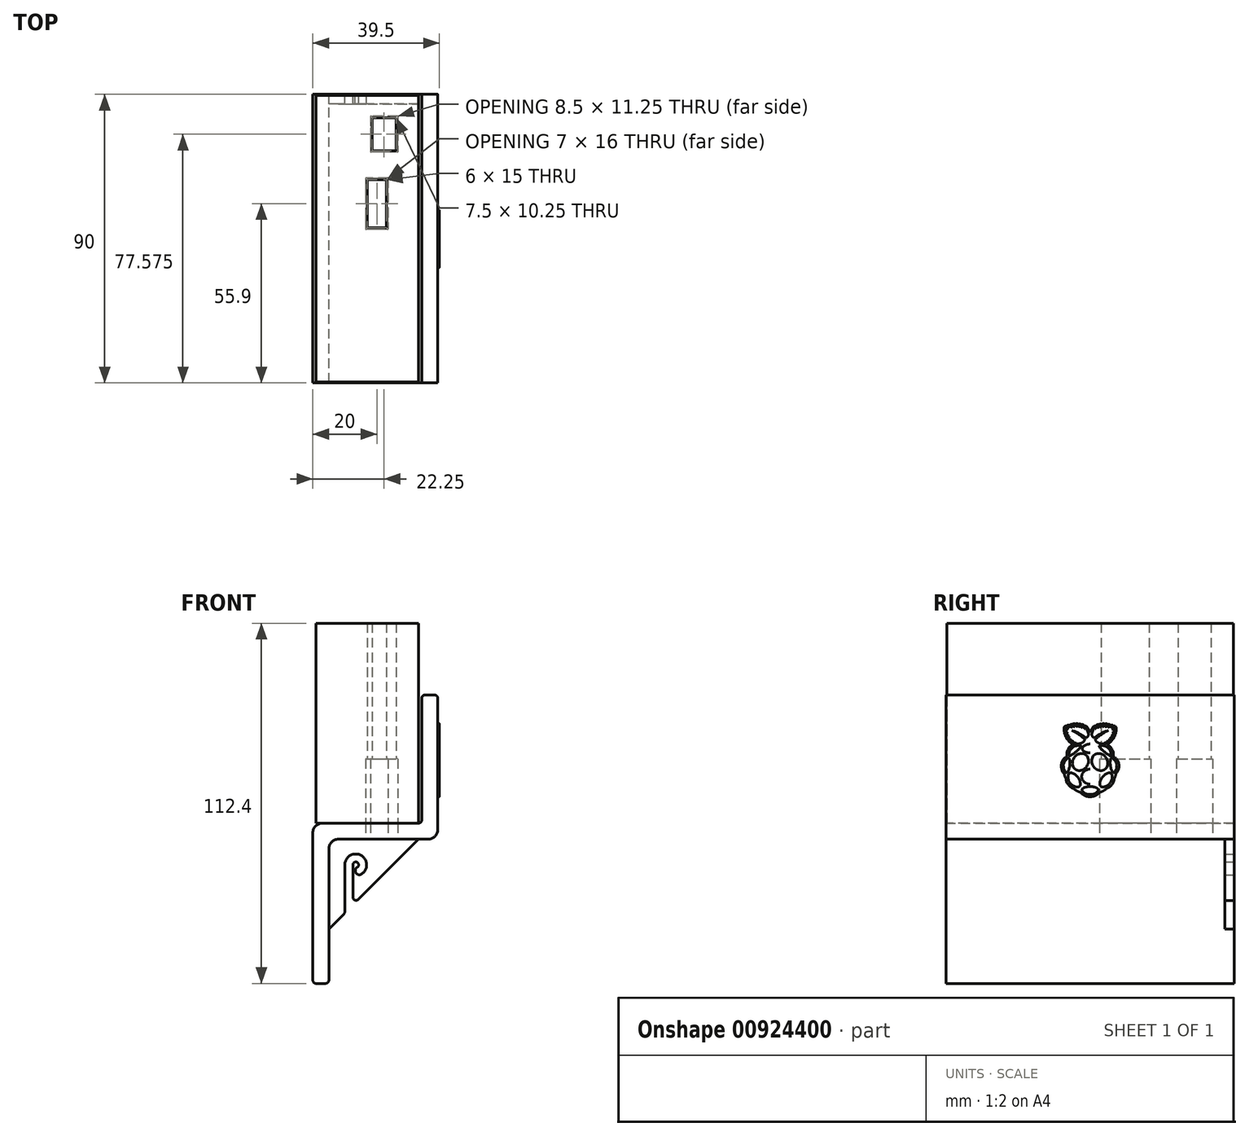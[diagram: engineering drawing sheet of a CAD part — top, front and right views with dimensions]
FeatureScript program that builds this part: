
annotation { "Feature Type Name" : "Feature", "Feature Type Description" : "" }
export const myFeature = defineFeature(function(context is Context, id is Id, definition is map)
    precondition{}
    {
        {
            var Q0;
            Q0=qCreatedBy(makeId("Front.planeOp"),FACE);
            var sketch = newSketch(context, id + "F0", { "sketchPlane" : qUnion([Q0])});
            skLineSegment(sketch, "E0", {"start": v(17, 44) * mm, "end": v(17, 6) * mm});
            skLineSegment(sketch, "E1", {"start": v(16, 5) * mm, "end": v(-14, 5) * mm});
            skLineSegment(sketch, "E2", {"start": v(-17, 2) * mm, "end": v(-17, -44) * mm});
            skLineSegment(sketch, "E3", {"start": v(-16, -45) * mm, "end": v(-13, -45) * mm});
            skLineSegment(sketch, "E4", {"start": v(-12, -44) * mm, "end": v(-12, -3) * mm});
            skLineSegment(sketch, "E5", {"start": v(-9, 0) * mm, "end": v(19, 0) * mm});
            skLineSegment(sketch, "E6", {"start": v(22, 3) * mm, "end": v(22, 44) * mm});
            skLineSegment(sketch, "E7", {"start": v(21, 45) * mm, "end": v(18, 45) * mm});
            skPoint(sketch, "E8.visualSharp", {"position": v(-12, 0) * mm});
            skArc(sketch, "E8.filletArc", {"start": v(-9, 0) * mm, "mid": v(-11.12, -0.88) * mm, "end": v(-12, -3) * mm});
            skPoint(sketch, "E9.visualSharp", {"position": v(17, 5) * mm});
            skArc(sketch, "E9.filletArc", {"start": v(16, 5) * mm, "mid": v(16.7, 5.3) * mm, "end": v(17, 6) * mm});
            skPoint(sketch, "E10.visualSharp", {"position": v(22, 0) * mm});
            skArc(sketch, "E10.filletArc", {"start": v(19, 0) * mm, "mid": v(21.12, 0.88) * mm, "end": v(22, 3) * mm});
            skPoint(sketch, "E11.visualSharp", {"position": v(-17, 5) * mm});
            skArc(sketch, "E11.filletArc", {"start": v(-14, 5) * mm, "mid": v(-16.12, 4.12) * mm, "end": v(-17, 2) * mm});
            skPoint(sketch, "E12.visualSharp", {"position": v(22, 45) * mm});
            skArc(sketch, "E12.filletArc", {"start": v(22, 44) * mm, "mid": v(21.7, 44.7) * mm, "end": v(21, 45) * mm});
            skPoint(sketch, "E13.visualSharp", {"position": v(17, 45) * mm});
            skArc(sketch, "E13.filletArc", {"start": v(18, 45) * mm, "mid": v(17.3, 44.7) * mm, "end": v(17, 44) * mm});
            skPoint(sketch, "E14.visualSharp", {"position": v(-17, -45) * mm});
            skArc(sketch, "E14.filletArc", {"start": v(-17, -44) * mm, "mid": v(-16.7, -44.7) * mm, "end": v(-16, -45) * mm});
            skPoint(sketch, "E15.visualSharp", {"position": v(-12, -45) * mm});
            skArc(sketch, "E15.filletArc", {"start": v(-13, -45) * mm, "mid": v(-12.3, -44.7) * mm, "end": v(-12, -44) * mm});
            skSolve(sketch);
        }
        {
            var Q0;
            Q0=makeQuery(id+"F0.imprint","IMPRINT",FACE,{"disambiguationData":[TD([[makeQuery(id+"F0.imprint","IMPRINT",EDGE,{"derivedFrom":sQuery(id+"F0.wireOp",EDGE,"E0")}),1.0]])]});
            extrude(context, id + "F1", {"entities" : qUnion([Q0]), "endBound" : BoundingType.SYMMETRIC, "depth" : 90 * mm, "offsetDistance" : 25 * mm});
        }
        {
            var Q0;
            Q0=makeQuery(id+"F1.opExtrude","CAP_FACE",FACE,{"disambiguationData":[OSD([sQuery(id+"F0.wireOp",EDGE,"E0"),sQuery(id+"F0.wireOp",EDGE,"E1"),sQuery(id+"F0.wireOp",EDGE,"E2"),sQuery(id+"F0.wireOp",EDGE,"E3"),sQuery(id+"F0.wireOp",EDGE,"E4"),sQuery(id+"F0.wireOp",EDGE,"E5"),sQuery(id+"F0.wireOp",EDGE,"E6"),sQuery(id+"F0.wireOp",EDGE,"E7"),sQuery(id+"F0.wireOp",EDGE,"E8.filletArc"),sQuery(id+"F0.wireOp",EDGE,"E9.filletArc"),sQuery(id+"F0.wireOp",EDGE,"E10.filletArc"),sQuery(id+"F0.wireOp",EDGE,"E11.filletArc"),sQuery(id+"F0.wireOp",EDGE,"E12.filletArc"),sQuery(id+"F0.wireOp",EDGE,"E13.filletArc"),sQuery(id+"F0.wireOp",EDGE,"E14.filletArc"),sQuery(id+"F0.wireOp",EDGE,"E15.filletArc")])],"isStart":true});
            var sketch = newSketch(context, id + "F2", { "sketchPlane" : qUnion([Q0])});
            skLineSegment(sketch, "E16.0", {"start": v(9, 0) * mm, "end": v(-19, 0) * mm});
            skPoint(sketch, "E17.0", {"position": v(11.12, -0.88) * mm});
            skLineSegment(sketch, "E18.0", {"start": v(12, -44) * mm, "end": v(12, -3) * mm});
            skArc(sketch, "E19.0", {"start": v(9, 0) * mm, "mid": v(11.12, -0.88) * mm, "end": v(12, -3) * mm});
            skLineSegment(sketch, "E20", {"start": v(-16, 0) * mm, "end": v(12, -28) * mm, "construction": true});
            skLineSegment(sketch, "E21", {"start": v(4.5, -20.5) * mm, "end": v(4.5, -8) * mm});
            skArc(sketch, "E22", {"start": v(4.5, -8) * mm, "mid": v(3.16, -7.22) * mm, "end": v(3.14, -8.77) * mm});
            skArc(sketch, "E23.0", {"start": v(7, -8) * mm, "mid": v(1.93, -5.04) * mm, "end": v(1.86, -10.92) * mm});
            skArc(sketch, "E24", {"start": v(1.86, -10.92) * mm, "mid": v(3.57, -10.48) * mm, "end": v(3.14, -8.77) * mm});
            skLineSegment(sketch, "E25", {"start": v(7, -8) * mm, "end": v(7, -23) * mm});
            skLineSegment(sketch, "E26", {"start": v(-16, 0) * mm, "end": v(4.5, -20.5) * mm});
            skLineSegment(sketch, "E27", {"start": v(7, -23) * mm, "end": v(12, -28) * mm});
            skSolve(sketch);
        }
        {
            var Q0;
            {var subQ0=sQuery(id+"F2.wireOp",EDGE,"E19.0");Q0=makeQuery(id+"F2.imprint","IMPRINT",FACE,{"disambiguationData":[TD([[makeQuery(id+"F2.imprint","IMPRINT",EDGE,{"derivedFrom":subQ0}),-1.0]])]});}
            extrude(context, id + "F3", {"entities" : qUnion([Q0]), "operationType" : NewBodyOperationType.ADD, "oppositeDirection" : true, "depth" : 3 * mm, "offsetDistance" : 25 * mm});
        }
        {
            var Q0;
            Q0=makeQuery(id+"F1.opExtrude","SWEPT_FACE",FACE,{"disambiguationData":[OSD([sQuery(id+"F0.wireOp",EDGE,"E1")])]});
            var sketch = newSketch(context, id + "F4", { "sketchPlane" : qUnion([Q0])});
            skLineSegment(sketch, "E28.bottom", {"start": v(16, 44.7) * mm, "end": v(-16, 44.7) * mm});
            skLineSegment(sketch, "E28.top", {"start": v(16, -44.7) * mm, "end": v(-16, -44.7) * mm});
            skLineSegment(sketch, "E28.left", {"start": v(16, 44.7) * mm, "end": v(16, -44.7) * mm});
            skLineSegment(sketch, "E28.right", {"start": v(-16, 44.7) * mm, "end": v(-16, -44.7) * mm});
            skLineSegment(sketch, "E29.bottom", {"start": v(9, 37.7) * mm, "end": v(1.5, 37.7) * mm});
            skLineSegment(sketch, "E29.top", {"start": v(9, 27.45) * mm, "end": v(1.5, 27.45) * mm});
            skLineSegment(sketch, "E29.left", {"start": v(9, 37.7) * mm, "end": v(9, 27.45) * mm});
            skLineSegment(sketch, "E29.right", {"start": v(1.5, 37.7) * mm, "end": v(1.5, 27.45) * mm});
            skLineSegment(sketch, "E30.bottom", {"start": v(6, 18.4) * mm, "end": v(0, 18.4) * mm});
            skLineSegment(sketch, "E30.top", {"start": v(6, 3.4) * mm, "end": v(0, 3.4) * mm});
            skLineSegment(sketch, "E30.left", {"start": v(6, 18.4) * mm, "end": v(6, 3.4) * mm});
            skLineSegment(sketch, "E30.right", {"start": v(0, 18.4) * mm, "end": v(0, 3.4) * mm});
            skSolve(sketch);
        }
        {
            var Q0;
            Q0 = qSketchRegion(id + "F4", true);
            extrude(context, id + "F5", {"entities" : qUnion([Q0]), "depth" : 62.4 * mm, "offsetDistance" : 25 * mm});
        }
        {
            var Q0;
            Q0=makeQuery(id+"F3.opExtrude","SWEPT_EDGE",EDGE,{"disambiguationData":[OSD([sQuery(id+"F2.wireOp",EDGE,"E25"),sQuery(id+"F2.wireOp",EDGE,"E27")])]});
            var Q1;
            Q1=makeQuery(id+"F3.opExtrude","SWEPT_EDGE",EDGE,{"disambiguationData":[OSD([sQuery(id+"F2.wireOp",EDGE,"E18.0"),sQuery(id+"F2.wireOp",EDGE,"E27")])]});
            var Q2;
            Q2=makeQuery(id+"F3.opExtrude","SWEPT_EDGE",EDGE,{"disambiguationData":[OSD([sQuery(id+"F2.wireOp",EDGE,"E21"),sQuery(id+"F2.wireOp",EDGE,"E26")])]});
            var Q3;
            Q3=makeQuery(id+"F3.opExtrude","SWEPT_EDGE",EDGE,{"disambiguationData":[OSD([sQuery(id+"F2.wireOp",EDGE,"E16.0"),sQuery(id+"F2.wireOp",EDGE,"E26")])]});
            fillet(context, id + "F6", {"entities" : qUnion([Q0, Q1, Q2, Q3]), "radius" : 1 * mm, "tangentPropagation" : true, "allowEdgeOverflow" : false});
        }
        {
            var Q0;
            Q0=makeQuery(id+"F1.opExtrude","SWEPT_FACE",FACE,{"disambiguationData":[OSD([sQuery(id+"F0.wireOp",EDGE,"E5")])]});
            var sketch = newSketch(context, id + "F7", { "sketchPlane" : qUnion([Q0])});
            skLineSegment(sketch, "E31.0.0", {"start": v(-9, -42) * mm, "end": v(16.41, -42) * mm, "construction": true});
            skLineSegment(sketch, "E31.0.1", {"start": v(16.41, -42) * mm, "end": v(16.41, -45) * mm});
            skLineSegment(sketch, "E31.0.2", {"start": v(16.41, -45) * mm, "end": v(19, -45) * mm});
            skLineSegment(sketch, "E31.0.3", {"start": v(19, -45) * mm, "end": v(19, 45) * mm, "construction": true});
            skLineSegment(sketch, "E31.0.4", {"start": v(19, 45) * mm, "end": v(-9, 45) * mm, "construction": true});
            skLineSegment(sketch, "E32.0", {"start": v(15.7, -45) * mm, "end": v(-2.8, -45) * mm});
            skLineSegment(sketch, "E33.0", {"start": v(17, 45) * mm, "end": v(17, -45) * mm, "construction": true});
            skLineSegment(sketch, "E34.right", {"start": v(-16, 44.7) * mm, "end": v(-16, -44.7) * mm, "construction": true});
            skLineSegment(sketch, "E35.0.0", {"start": v(-16, 44.7) * mm, "end": v(16, 44.7) * mm, "construction": true});
            skLineSegment(sketch, "E35.0.1", {"start": v(16, 44.7) * mm, "end": v(16, -44.7) * mm, "construction": true});
            skLineSegment(sketch, "E35.0.2", {"start": v(16, -44.7) * mm, "end": v(-16, -44.7) * mm, "construction": true});
            skLineSegment(sketch, "E35.0.3", {"start": v(-16, -44.7) * mm, "end": v(-16, 44.7) * mm, "construction": true});
            skLineSegment(sketch, "E36.0.0", {"start": v(16, 44.7) * mm, "end": v(-16, 44.7) * mm, "construction": true});
            skLineSegment(sketch, "E36.0.2", {"start": v(-16, -44.7) * mm, "end": v(16, -44.7) * mm, "construction": true});
            skLineSegment(sketch, "E36.0.3", {"start": v(16, -44.7) * mm, "end": v(16, 44.7) * mm});
            skLineSegment(sketch, "E37.0", {"start": v(6, -3.4) * mm, "end": v(0, -3.4) * mm, "construction": true});
            skLineSegment(sketch, "E38.0", {"start": v(6, -18.4) * mm, "end": v(6, -3.4) * mm, "construction": true});
            skLineSegment(sketch, "E39.0", {"start": v(0, -18.4) * mm, "end": v(0, -3.4) * mm, "construction": true});
            skLineSegment(sketch, "E40.0", {"start": v(9, -27.45) * mm, "end": v(1.5, -27.45) * mm, "construction": true});
            skLineSegment(sketch, "E41.0", {"start": v(1.5, -37.7) * mm, "end": v(1.5, -27.45) * mm, "construction": true});
            skLineSegment(sketch, "E42.0", {"start": v(9, -37.7) * mm, "end": v(1.5, -37.7) * mm, "construction": true});
            skLineSegment(sketch, "E43.0", {"start": v(6, -18.4) * mm, "end": v(0, -18.4) * mm, "construction": true});
            skLineSegment(sketch, "E44.bottom", {"start": v(1.1, -26.95) * mm, "end": v(9.4, -26.95) * mm});
            skLineSegment(sketch, "E44.top", {"start": v(1.1, -38.2) * mm, "end": v(9.4, -38.2) * mm});
            skLineSegment(sketch, "E44.left", {"start": v(1, -27.05) * mm, "end": v(1, -38.1) * mm});
            skLineSegment(sketch, "E44.right", {"start": v(9.5, -27.05) * mm, "end": v(9.5, -38.1) * mm});
            skLineSegment(sketch, "E45.bottom", {"start": v(-0.4, -2.9) * mm, "end": v(6.4, -2.9) * mm});
            skLineSegment(sketch, "E45.top", {"start": v(-0.4, -18.9) * mm, "end": v(6.4, -18.9) * mm});
            skLineSegment(sketch, "E45.left", {"start": v(-0.5, -3) * mm, "end": v(-0.5, -18.8) * mm});
            skLineSegment(sketch, "E45.right", {"start": v(6.5, -3) * mm, "end": v(6.5, -18.8) * mm});
            skPoint(sketch, "E46.visualSharp", {"position": v(-0.5, -2.9) * mm});
            skArc(sketch, "E46.filletArc", {"start": v(-0.4, -2.9) * mm, "mid": v(-0.47, -2.93) * mm, "end": v(-0.5, -3) * mm});
            skPoint(sketch, "E47.visualSharp", {"position": v(6.5, -2.9) * mm});
            skArc(sketch, "E47.filletArc", {"start": v(6.5, -3) * mm, "mid": v(6.47, -2.93) * mm, "end": v(6.4, -2.9) * mm});
            skPoint(sketch, "E48.visualSharp", {"position": v(6.5, -18.9) * mm});
            skArc(sketch, "E48.filletArc", {"start": v(6.4, -18.9) * mm, "mid": v(6.47, -18.87) * mm, "end": v(6.5, -18.8) * mm});
            skPoint(sketch, "E49.visualSharp", {"position": v(-0.5, -18.9) * mm});
            skArc(sketch, "E49.filletArc", {"start": v(-0.5, -18.8) * mm, "mid": v(-0.47, -18.87) * mm, "end": v(-0.4, -18.9) * mm});
            skPoint(sketch, "E50.visualSharp", {"position": v(1, -26.95) * mm});
            skArc(sketch, "E50.filletArc", {"start": v(1.1, -26.95) * mm, "mid": v(1.03, -26.98) * mm, "end": v(1, -27.05) * mm});
            skPoint(sketch, "E51.visualSharp", {"position": v(9.5, -26.95) * mm});
            skArc(sketch, "E51.filletArc", {"start": v(9.5, -27.05) * mm, "mid": v(9.47, -26.98) * mm, "end": v(9.4, -26.95) * mm});
            skPoint(sketch, "E52.visualSharp", {"position": v(9.5, -38.2) * mm});
            skArc(sketch, "E52.filletArc", {"start": v(9.4, -38.2) * mm, "mid": v(9.47, -38.17) * mm, "end": v(9.5, -38.1) * mm});
            skPoint(sketch, "E53.visualSharp", {"position": v(1, -38.2) * mm});
            skArc(sketch, "E53.filletArc", {"start": v(1, -38.1) * mm, "mid": v(1.03, -38.17) * mm, "end": v(1.1, -38.2) * mm});
            skSolve(sketch);
        }
        {
            var Q0;
            Q0=makeQuery(id+"F7.imprint","IMPRINT",FACE,{"disambiguationData":[TD([[makeQuery(id+"F7.imprint","IMPRINT",EDGE,{"derivedFrom":sQuery(id+"F7.wireOp",EDGE,"E45.bottom")}),-1.0]])]});
            var Q1;
            Q1=makeQuery(id+"F7.imprint","IMPRINT",FACE,{"disambiguationData":[TD([[makeQuery(id+"F7.imprint","IMPRINT",EDGE,{"derivedFrom":sQuery(id+"F7.wireOp",EDGE,"E44.bottom")}),-1.0]])]});
            extrude(context, id + "F8", {"entities" : qUnion([Q0, Q1]), "operationType" : NewBodyOperationType.REMOVE, "oppositeDirection" : true, "depth" : 25 * mm, "offsetDistance" : 25 * mm});
        }
        {
            var Q0;
            Q0=makeQuery(id+"F1.opExtrude","SWEPT_FACE",FACE,{"disambiguationData":[OSD([sQuery(id+"F0.wireOp",EDGE,"E6")])]});
            var sketch = newSketch(context, id + "F9", { "sketchPlane" : qUnion([Q0])});
            skEllipticalArc(sketch, "E54", {});
            skArc(sketch, "E55", {"start": v(-1.68, 31.17) * mm, "mid": v(-3.59, 32.72) * mm, "end": v(-5.72, 33.94) * mm});
            skArc(sketch, "E56", {"start": v(-1.32, 31.57) * mm, "mid": v(-3.4, 32.98) * mm, "end": v(-5.72, 33.94) * mm});
            skArc(sketch, "E57", {"start": v(-7.68, 33.94) * mm, "mid": v(-7.38, 33.53) * mm, "end": v(-7, 33.2) * mm});
            skEllipticalArc(sketch, "E58", {});
            skArc(sketch, "E59", {"start": v(5.72, 33.94) * mm, "mid": v(3.59, 32.72) * mm, "end": v(1.68, 31.17) * mm});
            skArc(sketch, "E60", {"start": v(5.72, 33.94) * mm, "mid": v(3.4, 32.98) * mm, "end": v(1.32, 31.57) * mm});
            skArc(sketch, "E61", {"start": v(7, 33.2) * mm, "mid": v(7.38, 33.53) * mm, "end": v(7.68, 33.94) * mm});
            skFitSpline(sketch, "E62", {"points": [v(-5.2, 29.54) * mm, v(-5.32, 29.49) * mm, v(-5.66, 29.33) * mm, v(-6.1, 28.97) * mm, v(-6.55, 28.55) * mm, v(-6.84, 28.05) * mm, v(-7.08, 27.57) * mm, v(-7.23, 27.05) * mm, v(-7.28, 26.56) * mm, v(-7.28, 26.22) * mm, v(-7.28, 26.05) * mm]});
            skFitSpline(sketch, "E63", {"points": [v(-7.28, 26.05) * mm, v(-7.3, 26) * mm, v(-7.36, 25.88) * mm, v(-7.4, 25.76) * mm, v(-7.41, 25.7) * mm]});
            skFitSpline(sketch, "E64", {"points": [v(-7.41, 25.7) * mm, v(-7.55, 25.61) * mm, v(-7.88, 25.41) * mm, v(-8.27, 25) * mm, v(-8.6, 24.44) * mm, v(-8.87, 23.87) * mm, v(-8.97, 23.25) * mm, v(-9, 22.67) * mm, v(-8.93, 22.16) * mm, v(-8.8, 21.67) * mm, v(-8.61, 21.23) * mm, v(-8.37, 20.8) * mm, v(-8.16, 20.59) * mm, v(-8.06, 20.5) * mm]});
            skFitSpline(sketch, "E65", {"points": [v(-8.06, 20.5) * mm, v(-8, 20.22) * mm, v(-7.88, 19.68) * mm, v(-7.67, 19.17) * mm, v(-7.57, 18.93) * mm]});
            skFitSpline(sketch, "E66", {"points": [v(-7.57, 18.93) * mm, v(-7.5, 18.6) * mm, v(-7.4, 18.1) * mm, v(-7.14, 17.5) * mm, v(-6.85, 17.1) * mm, v(-6.57, 16.74) * mm, v(-6.25, 16.44) * mm, v(-5.92, 16.21) * mm, v(-5.56, 15.98) * mm, v(-5.3, 15.88) * mm, v(-5.15, 15.82) * mm]});
            skFitSpline(sketch, "E67", {"points": [v(-5.15, 15.82) * mm, v(-5, 15.7) * mm, v(-4.76, 15.5) * mm, v(-4.36, 15.25) * mm, v(-3.95, 15.01) * mm, v(-3.44, 14.77) * mm, v(-3.06, 14.63) * mm, v(-2.86, 14.55) * mm]});
            skFitSpline(sketch, "E68", {"points": [v(-2.86, 14.55) * mm, v(-2.8, 14.46) * mm, v(-2.64, 14.25) * mm, v(-2.3, 14) * mm, v(-1.89, 13.73) * mm, v(-1.47, 13.52) * mm, v(-1.02, 13.38) * mm, v(-0.59, 13.3) * mm, v(-0.24, 13.27) * mm, v(-0.05, 13.27) * mm, v(0, 13.27) * mm]});
            skFitSpline(sketch, "E69", {"points": [v(-2.86, 29.07) * mm, v(-2.99, 29.11) * mm, v(-3.34, 29.22) * mm, v(-3.84, 29.23) * mm, v(-4.4, 29.14) * mm, v(-4.88, 28.98) * mm, v(-5.34, 28.74) * mm, v(-5.67, 28.44) * mm, v(-5.95, 28.14) * mm, v(-6.17, 27.84) * mm, v(-6.34, 27.52) * mm, v(-6.48, 27.17) * mm, v(-6.57, 26.73) * mm, v(-6.6, 26.33) * mm, v(-6.58, 26.1) * mm, v(-6.58, 26.02) * mm]});
            skFitSpline(sketch, "E70", {"points": [v(-6.58, 26.02) * mm, v(-6.57, 26) * mm, v(-6.55, 25.97) * mm, v(-6.45, 25.96) * mm, v(-6.33, 26) * mm, v(-6.1, 26.08) * mm, v(-5.71, 26.34) * mm, v(-5.04, 26.73) * mm, v(-4.36, 27.34) * mm, v(-3.67, 27.94) * mm, v(-3.24, 28.41) * mm, v(-2.98, 28.73) * mm, v(-2.89, 28.88) * mm, v(-2.85, 28.96) * mm, v(-2.84, 29.01) * mm, v(-2.83, 29.06) * mm, v(-2.85, 29.07) * mm, v(-2.86, 29.07) * mm]});
            skFitSpline(sketch, "E71", {"points": [v(0, 29.7) * mm, v(-0.08, 29.7) * mm, v(-0.28, 29.7) * mm, v(-0.65, 29.66) * mm, v(-1.02, 29.54) * mm, v(-1.38, 29.4) * mm, v(-1.68, 29.22) * mm, v(-1.98, 29.01) * mm, v(-2.2, 28.8) * mm, v(-2.35, 28.6) * mm, v(-2.4, 28.42) * mm, v(-2.42, 28.3) * mm, v(-2.42, 28.14) * mm, v(-2.4, 27.99) * mm, v(-2.3, 27.82) * mm, v(-2.18, 27.65) * mm, v(-2, 27.49) * mm, v(-1.77, 27.35) * mm, v(-1.5, 27.2) * mm, v(-1.22, 27.1) * mm, v(-0.91, 27.01) * mm, v(-0.58, 26.95) * mm, v(-0.27, 26.92) * mm, v(-0.07, 26.91) * mm, v(0, 26.91) * mm]});
            skFitSpline(sketch, "E72", {"points": [v(-6.85, 25.27) * mm, v(-7, 25.18) * mm, v(-7.37, 24.94) * mm, v(-7.82, 24.47) * mm, v(-8.1, 23.88) * mm, v(-8.31, 23.3) * mm, v(-8.3, 22.72) * mm, v(-8.23, 22.17) * mm, v(-8.1, 21.75) * mm, v(-7.95, 21.5) * mm, v(-7.88, 21.38) * mm]});
            skFitSpline(sketch, "E73", {"points": [v(-6.85, 25.27) * mm, v(-6.83, 25.27) * mm, v(-6.78, 25.3) * mm, v(-6.69, 25.28) * mm, v(-6.6, 25.22) * mm, v(-6.5, 25.11) * mm, v(-6.46, 25.02) * mm, v(-6.44, 24.97) * mm]});
            skFitSpline(sketch, "E74", {"points": [v(-6.44, 24.97) * mm, v(-6.41, 24.89) * mm, v(-6.35, 24.73) * mm, v(-6.3, 24.48) * mm, v(-6.3, 24.21) * mm, v(-6.3, 23.9) * mm, v(-6.3, 23.57) * mm, v(-6.31, 23.18) * mm, v(-6.38, 22.74) * mm, v(-6.46, 22.27) * mm, v(-6.59, 21.85) * mm, v(-6.73, 21.5) * mm, v(-6.85, 21.21) * mm, v(-7, 21.01) * mm, v(-7.1, 20.88) * mm, v(-7.23, 20.82) * mm, v(-7.3, 20.78) * mm, v(-7.37, 20.77) * mm, v(-7.4, 20.8) * mm, v(-7.45, 20.81) * mm, v(-7.52, 20.89) * mm, v(-7.63, 21) * mm, v(-7.73, 21.15) * mm, v(-7.82, 21.27) * mm, v(-7.86, 21.35) * mm, v(-7.88, 21.38) * mm]});
            skFitSpline(sketch, "E75", {"points": [v(0, 16.41) * mm, v(0, 16.41) * mm, v(0, 16.41) * mm, v(0, 16.41) * mm, v(-0.32, 16.41) * mm, v(-0.7, 16.38) * mm, v(-1.13, 16.3) * mm, v(-1.53, 16.22) * mm, v(-1.85, 16.1) * mm, v(-2.1, 16) * mm, v(-2.26, 15.87) * mm, v(-2.42, 15.75) * mm, v(-2.52, 15.63) * mm, v(-2.59, 15.5) * mm, v(-2.59, 15.38) * mm, v(-2.56, 15.27) * mm, v(-2.53, 15.21) * mm, v(-2.51, 15.18) * mm]});
            skFitSpline(sketch, "E76", {"points": [v(-2.51, 15.18) * mm, v(-2.49, 15.13) * mm, v(-2.44, 15.05) * mm, v(-2.31, 14.93) * mm, v(-2.18, 14.77) * mm, v(-1.99, 14.6) * mm, v(-1.79, 14.46) * mm, v(-1.57, 14.33) * mm, v(-1.38, 14.22) * mm, v(-1.2, 14.15) * mm, v(-1.01, 14.08) * mm, v(-0.75, 14.02) * mm, v(-0.45, 13.96) * mm, v(-0.19, 13.96) * mm, v(-0.04, 13.97) * mm, v(0, 13.97) * mm]});
            skFitSpline(sketch, "E77", {"points": [v(-6.3, 20.66) * mm, v(-6.23, 20.68) * mm, v(-6.03, 20.73) * mm, v(-5.7, 20.7) * mm, v(-5.36, 20.59) * mm, v(-5.06, 20.45) * mm, v(-4.78, 20.3) * mm, v(-4.51, 20.09) * mm, v(-4.28, 19.85) * mm, v(-4.06, 19.62) * mm, v(-3.86, 19.37) * mm, v(-3.66, 19.13) * mm, v(-3.5, 18.84) * mm, v(-3.34, 18.56) * mm, v(-3.21, 18.26) * mm, v(-3.12, 17.94) * mm, v(-3.05, 17.6) * mm, v(-3.03, 17.28) * mm, v(-3.06, 17.01) * mm, v(-3.14, 16.75) * mm, v(-3.31, 16.51) * mm, v(-3.5, 16.35) * mm, v(-3.64, 16.31) * mm, v(-3.68, 16.3) * mm]});
            skFitSpline(sketch, "E78", {"points": [v(-3.68, 16.3) * mm, v(-3.73, 16.3) * mm, v(-3.9, 16.3) * mm, v(-4.17, 16.31) * mm, v(-4.52, 16.35) * mm, v(-4.83, 16.47) * mm, v(-5.15, 16.57) * mm, v(-5.46, 16.77) * mm, v(-5.8, 17) * mm, v(-6.1, 17.33) * mm, v(-6.4, 17.7) * mm, v(-6.62, 18.08) * mm, v(-6.75, 18.46) * mm, v(-6.84, 18.82) * mm, v(-6.88, 19.2) * mm, v(-6.9, 19.58) * mm, v(-6.83, 19.95) * mm, v(-6.74, 20.24) * mm, v(-6.6, 20.45) * mm, v(-6.46, 20.59) * mm, v(-6.34, 20.64) * mm, v(-6.3, 20.66) * mm]});
            skFitSpline(sketch, "E79", {"points": [v(-3.44, 26.63) * mm, v(-3.54, 26.6) * mm, v(-3.76, 26.5) * mm, v(-4.1, 26.31) * mm, v(-4.47, 26.07) * mm, v(-4.74, 25.7) * mm, v(-5.05, 25.37) * mm, v(-5.27, 24.93) * mm, v(-5.45, 24.47) * mm, v(-5.5, 23.98) * mm, v(-5.51, 23.46) * mm, v(-5.4, 22.93) * mm, v(-5.17, 22.34) * mm, v(-4.76, 21.89) * mm, v(-4.25, 21.6) * mm, v(-3.72, 21.45) * mm, v(-3.2, 21.4) * mm, v(-2.85, 21.47) * mm, v(-2.7, 21.52) * mm]});
            skFitSpline(sketch, "E80", {"points": [v(-2.7, 21.52) * mm, v(-2.67, 21.52) * mm, v(-2.5, 21.57) * mm, v(-2.14, 21.71) * mm, v(-1.68, 22.08) * mm, v(-1.23, 22.5) * mm, v(-0.88, 23.04) * mm, v(-0.62, 23.65) * mm, v(-0.51, 24.3) * mm, v(-0.53, 24.94) * mm, v(-0.72, 25.54) * mm, v(-1.04, 26.05) * mm, v(-1.46, 26.39) * mm, v(-1.82, 26.6) * mm, v(-2.16, 26.7) * mm, v(-2.45, 26.74) * mm, v(-2.7, 26.76) * mm, v(-2.97, 26.75) * mm, v(-3.15, 26.7) * mm, v(-3.44, 26.63) * mm]});
            skFitSpline(sketch, "E81", {"points": [v(-5.2, 29.54) * mm, v(-5.2, 29.56) * mm, v(-5.26, 29.6) * mm, v(-5.42, 29.62) * mm, v(-5.6, 29.7) * mm, v(-5.8, 29.77) * mm, v(-5.93, 29.9) * mm, v(-5.99, 30.02) * mm, v(-6.02, 30.1) * mm, v(-6, 30.15) * mm, v(-6, 30.17) * mm]});
            skFitSpline(sketch, "E82", {"points": [v(-6, 30.17) * mm, v(-6.11, 30.21) * mm, v(-6.3, 30.28) * mm, v(-6.53, 30.43) * mm, v(-6.68, 30.58) * mm, v(-6.74, 30.74) * mm, v(-6.75, 30.83) * mm, v(-6.75, 30.88) * mm]});
            skFitSpline(sketch, "E83", {"points": [v(-6.75, 30.88) * mm, v(-6.84, 30.94) * mm, v(-6.99, 31.05) * mm, v(-7.16, 31.21) * mm, v(-7.3, 31.34) * mm, v(-7.35, 31.49) * mm, v(-7.37, 31.61) * mm, v(-7.36, 31.7) * mm, v(-7.35, 31.74) * mm]});
            skFitSpline(sketch, "E84", {"points": [v(-7.35, 31.74) * mm, v(-7.41, 31.79) * mm, v(-7.52, 31.88) * mm, v(-7.63, 32.03) * mm, v(-7.7, 32.17) * mm, v(-7.73, 32.32) * mm, v(-7.73, 32.46) * mm, v(-7.72, 32.54) * mm, v(-7.72, 32.58) * mm]});
            skFitSpline(sketch, "E85", {"points": [v(-7.72, 32.58) * mm, v(-7.77, 32.64) * mm, v(-7.87, 32.75) * mm, v(-7.97, 32.91) * mm, v(-8.01, 33.07) * mm, v(-8, 33.19) * mm, v(-8.02, 33.3) * mm, v(-7.99, 33.38) * mm, v(-7.97, 33.41) * mm]});
            skFitSpline(sketch, "E86", {"points": [v(-7.97, 33.41) * mm, v(-8.02, 33.48) * mm, v(-8.1, 33.6) * mm, v(-8.15, 33.78) * mm, v(-8.17, 33.93) * mm, v(-8.16, 34.09) * mm, v(-8.12, 34.22) * mm, v(-8.05, 34.3) * mm, v(-8.01, 34.35) * mm, v(-8, 34.36) * mm]});
            skFitSpline(sketch, "E87", {"points": [v(-8, 34.36) * mm, v(-8.02, 34.39) * mm, v(-8.06, 34.43) * mm, v(-8.1, 34.53) * mm, v(-8.12, 34.64) * mm, v(-8.12, 34.77) * mm, v(-8.13, 34.91) * mm, v(-8.05, 35.05) * mm, v(-7.96, 35.16) * mm, v(-7.84, 35.24) * mm, v(-7.72, 35.28) * mm, v(-7.59, 35.3) * mm, v(-7.46, 35.3) * mm, v(-7.36, 35.28) * mm, v(-7.3, 35.27) * mm, v(-7.3, 35.27) * mm]});
            skFitSpline(sketch, "E88", {"points": [v(-7.3, 35.27) * mm, v(-7.28, 35.3) * mm, v(-7.24, 35.36) * mm, v(-7.17, 35.44) * mm, v(-7.08, 35.53) * mm, v(-6.97, 35.56) * mm, v(-6.83, 35.6) * mm, v(-6.66, 35.6) * mm, v(-6.45, 35.61) * mm, v(-6.3, 35.6) * mm, v(-6.23, 35.6) * mm]});
            skFitSpline(sketch, "E89", {"points": [v(0, 33.27) * mm, v(-0.04, 33.38) * mm, v(-0.14, 33.6) * mm, v(-0.27, 33.94) * mm, v(-0.42, 34.26) * mm, v(-0.62, 34.56) * mm, v(-0.8, 34.83) * mm, v(-1, 35.05) * mm, v(-1.18, 35.22) * mm, v(-1.36, 35.3) * mm, v(-1.5, 35.34) * mm, v(-1.62, 35.37) * mm, v(-1.68, 35.35) * mm, v(-1.7, 35.34) * mm]});
            skFitSpline(sketch, "E90", {"points": [v(-1.7, 35.34) * mm, v(-1.76, 35.4) * mm, v(-1.88, 35.5) * mm, v(-2.02, 35.64) * mm, v(-2.15, 35.75) * mm, v(-2.3, 35.77) * mm, v(-2.43, 35.8) * mm, v(-2.55, 35.78) * mm, v(-2.64, 35.76) * mm, v(-2.69, 35.75) * mm, v(-2.71, 35.74) * mm]});
            skFitSpline(sketch, "E91", {"points": [v(-2.71, 35.74) * mm, v(-2.78, 35.78) * mm, v(-2.88, 35.86) * mm, v(-3.04, 35.93) * mm, v(-3.18, 35.95) * mm, v(-3.3, 35.95) * mm, v(-3.43, 35.93) * mm, v(-3.5, 35.9) * mm, v(-3.54, 35.87) * mm]});
            skFitSpline(sketch, "E92", {"points": [v(-3.54, 35.87) * mm, v(-3.61, 35.9) * mm, v(-3.74, 35.96) * mm, v(-3.92, 36.03) * mm, v(-4.1, 36.06) * mm, v(-4.26, 36.07) * mm, v(-4.4, 36.02) * mm, v(-4.47, 35.96) * mm, v(-4.5, 35.93) * mm]});
            skFitSpline(sketch, "E93", {"points": [v(-4.5, 35.93) * mm, v(-4.57, 35.95) * mm, v(-4.7, 35.99) * mm, v(-4.9, 36.04) * mm, v(-5.07, 36.06) * mm, v(-5.22, 36) * mm, v(-5.35, 35.97) * mm, v(-5.43, 35.9) * mm, v(-5.46, 35.85) * mm, v(-5.48, 35.83) * mm]});
            skFitSpline(sketch, "E94", {"points": [v(-5.48, 35.83) * mm, v(-5.53, 35.84) * mm, v(-5.65, 35.86) * mm, v(-5.82, 35.85) * mm, v(-5.96, 35.82) * mm, v(-6.08, 35.78) * mm, v(-6.15, 35.72) * mm, v(-6.2, 35.67) * mm, v(-6.22, 35.62) * mm, v(-6.23, 35.6) * mm]});
            skFitSpline(sketch, "E95", {"points": [v(-1.68, 31.17) * mm, v(-1.7, 31.05) * mm, v(-1.74, 30.82) * mm, v(-1.93, 30.57) * mm, v(-2.1, 30.36) * mm, v(-2.33, 30.19) * mm, v(-2.6, 30.04) * mm, v(-2.94, 29.92) * mm, v(-3.3, 29.83) * mm, v(-3.7, 29.75) * mm, v(-4.09, 29.74) * mm, v(-4.41, 29.73) * mm, v(-4.59, 29.74) * mm, v(-4.63, 29.75) * mm]});
            skFitSpline(sketch, "E96", {"points": [v(-4.63, 29.75) * mm, v(-4.58, 29.78) * mm, v(-4.48, 29.84) * mm, v(-4.32, 29.9) * mm, v(-4.29, 29.98) * mm, v(-4.27, 30.01) * mm]});
            skFitSpline(sketch, "E97", {"points": [v(-4.27, 30.01) * mm, v(-4.34, 30.03) * mm, v(-4.48, 30.06) * mm, v(-4.72, 30.05) * mm, v(-4.97, 30.08) * mm, v(-5.2, 30.13) * mm, v(-5.41, 30.15) * mm, v(-5.48, 30.25) * mm, v(-5.5, 30.28) * mm]});
            skFitSpline(sketch, "E98", {"points": [v(-5.5, 30.28) * mm, v(-5.46, 30.29) * mm, v(-5.37, 30.3) * mm, v(-5.26, 30.33) * mm, v(-5.17, 30.36) * mm, v(-5.13, 30.42) * mm, v(-5.13, 30.46) * mm, v(-5.13, 30.47) * mm]});
            skFitSpline(sketch, "E99", {"points": [v(-5.13, 30.47) * mm, v(-5.17, 30.48) * mm, v(-5.27, 30.51) * mm, v(-5.42, 30.53) * mm, v(-5.61, 30.58) * mm, v(-5.83, 30.64) * mm, v(-6.03, 30.71) * mm, v(-6.2, 30.82) * mm, v(-6.23, 30.9) * mm, v(-6.24, 30.93) * mm]});
            skFitSpline(sketch, "E100", {"points": [v(-6.24, 30.93) * mm, v(-6.21, 30.92) * mm, v(-6.11, 30.89) * mm, v(-5.94, 30.88) * mm, v(-5.83, 30.94) * mm, v(-5.77, 30.97) * mm]});
            skFitSpline(sketch, "E101", {"points": [v(-5.77, 30.97) * mm, v(-5.97, 31.06) * mm, v(-6.35, 31.24) * mm, v(-6.68, 31.5) * mm, v(-6.85, 31.63) * mm]});
            skFitSpline(sketch, "E102", {"points": [v(-6.85, 31.63) * mm, v(-6.77, 31.63) * mm, v(-6.62, 31.63) * mm, v(-6.43, 31.6) * mm, v(-6.36, 31.67) * mm, v(-6.34, 31.69) * mm]});
            skFitSpline(sketch, "E103", {"points": [v(-6.34, 31.69) * mm, v(-6.49, 31.76) * mm, v(-6.81, 31.94) * mm, v(-7.07, 32.2) * mm, v(-7.21, 32.35) * mm]});
            skFitSpline(sketch, "E104", {"points": [v(-7.21, 32.35) * mm, v(-7.13, 32.36) * mm, v(-7, 32.36) * mm, v(-6.83, 32.35) * mm, v(-6.77, 32.39) * mm, v(-6.75, 32.4) * mm]});
            skFitSpline(sketch, "E105", {"points": [v(-6.75, 32.4) * mm, v(-6.88, 32.5) * mm, v(-7.17, 32.72) * mm, v(-7.38, 33.02) * mm, v(-7.5, 33.18) * mm]});
            skFitSpline(sketch, "E106", {"points": [v(-7.5, 33.18) * mm, v(-7.44, 33.17) * mm, v(-7.32, 33.15) * mm, v(-7.16, 33.14) * mm, v(-7.05, 33.16) * mm, v(-7.01, 33.2) * mm, v(-7, 33.2) * mm]});
            skFitSpline(sketch, "E107", {"points": [v(-7.68, 33.94) * mm, v(-7.6, 33.94) * mm, v(-7.47, 33.94) * mm, v(-7.3, 33.9) * mm, v(-7.2, 33.9) * mm, v(-7.14, 33.9) * mm]});
            skFitSpline(sketch, "E108", {"points": [v(-7.14, 33.9) * mm, v(-7.18, 34.03) * mm, v(-7.25, 34.25) * mm, v(-7.44, 34.5) * mm, v(-7.55, 34.66) * mm, v(-7.6, 34.73) * mm]});
            skFitSpline(sketch, "E109", {"points": [v(-7.6, 34.73) * mm, v(-7.46, 34.74) * mm, v(-7.22, 34.74) * mm, v(-6.91, 34.74) * mm, v(-6.7, 34.74) * mm, v(-6.6, 34.77) * mm, v(-6.56, 34.78) * mm]});
            skFitSpline(sketch, "E110", {"points": [v(-6.56, 34.78) * mm, v(-6.6, 34.83) * mm, v(-6.66, 34.92) * mm, v(-6.78, 34.99) * mm, v(-6.81, 35.05) * mm, v(-6.82, 35.06) * mm]});
            skFitSpline(sketch, "E111", {"points": [v(-6.82, 35.06) * mm, v(-6.74, 35.07) * mm, v(-6.52, 35.1) * mm, v(-6.2, 35.1) * mm, v(-5.9, 35.05) * mm, v(-5.73, 34.94) * mm, v(-5.63, 34.91) * mm, v(-5.6, 34.9) * mm]});
            skFitSpline(sketch, "E112", {"points": [v(-5.6, 34.9) * mm, v(-5.58, 34.95) * mm, v(-5.54, 35.04) * mm, v(-5.63, 35.15) * mm, v(-5.73, 35.22) * mm, v(-5.8, 35.27) * mm, v(-5.85, 35.3) * mm, v(-5.87, 35.32) * mm]});
            skFitSpline(sketch, "E113", {"points": [v(-5.87, 35.32) * mm, v(-5.78, 35.32) * mm, v(-5.61, 35.31) * mm, v(-5.41, 35.25) * mm, v(-5.24, 35.22) * mm, v(-5.09, 35.16) * mm, v(-4.94, 35.12) * mm, v(-4.84, 35.1) * mm, v(-4.79, 35.09) * mm, v(-4.77, 35.08) * mm]});
            skFitSpline(sketch, "E114", {"points": [v(-4.77, 35.08) * mm, v(-4.77, 35.12) * mm, v(-4.77, 35.19) * mm, v(-4.84, 35.3) * mm, v(-4.94, 35.36) * mm, v(-5.04, 35.43) * mm, v(-5.1, 35.46) * mm, v(-5.12, 35.48) * mm]});
            skFitSpline(sketch, "E115", {"points": [v(-5.12, 35.48) * mm, v(-5, 35.48) * mm, v(-4.79, 35.47) * mm, v(-4.52, 35.37) * mm, v(-4.3, 35.28) * mm, v(-4.15, 35.18) * mm, v(-4.06, 35.12) * mm, v(-4.02, 35.1) * mm]});
            skFitSpline(sketch, "E116", {"points": [v(-4.02, 35.1) * mm, v(-4, 35.14) * mm, v(-3.96, 35.23) * mm, v(-4.01, 35.35) * mm, v(-4.1, 35.44) * mm, v(-4.14, 35.5) * mm, v(-4.17, 35.53) * mm]});
            skFitSpline(sketch, "E117", {"points": [v(-4.17, 35.53) * mm, v(-4.12, 35.52) * mm, v(-4, 35.51) * mm, v(-3.85, 35.44) * mm, v(-3.71, 35.36) * mm, v(-3.6, 35.26) * mm, v(-3.46, 35.17) * mm, v(-3.35, 35.07) * mm, v(-3.28, 35.01) * mm, v(-3.25, 34.99) * mm]});
            skFitSpline(sketch, "E118", {"points": [v(-3.25, 34.99) * mm, v(-3.23, 35.03) * mm, v(-3.18, 35.12) * mm, v(-3.18, 35.28) * mm, v(-3.24, 35.37) * mm, v(-3.26, 35.42) * mm]});
            skFitSpline(sketch, "E119", {"points": [v(-3.26, 35.42) * mm, v(-3.2, 35.4) * mm, v(-3.1, 35.36) * mm, v(-2.94, 35.26) * mm, v(-2.81, 35.13) * mm, v(-2.73, 35.04) * mm, v(-2.7, 35) * mm]});
            skFitSpline(sketch, "E120", {"points": [v(-2.7, 35) * mm, v(-2.67, 34.98) * mm, v(-2.62, 34.91) * mm, v(-2.57, 34.84) * mm, v(-2.54, 34.8) * mm]});
            skFitSpline(sketch, "E121", {"points": [v(-2.54, 34.8) * mm, v(-2.51, 34.85) * mm, v(-2.46, 34.93) * mm, v(-2.42, 35.07) * mm, v(-2.45, 35.18) * mm, v(-2.46, 35.24) * mm, v(-2.46, 35.26) * mm]});
            skFitSpline(sketch, "E122", {"points": [v(-2.46, 35.26) * mm, v(-2.4, 35.22) * mm, v(-2.26, 35.14) * mm, v(-2.1, 34.95) * mm, v(-1.95, 34.78) * mm, v(-1.8, 34.63) * mm, v(-1.74, 34.52) * mm, v(-1.7, 34.46) * mm]});
            skFitSpline(sketch, "E123", {"points": [v(-1.7, 34.46) * mm, v(-1.68, 34.5) * mm, v(-1.61, 34.59) * mm, v(-1.58, 34.72) * mm, v(-1.58, 34.8) * mm, v(-1.58, 34.82) * mm]});
            skFitSpline(sketch, "E124", {"points": [v(-1.58, 34.82) * mm, v(-1.53, 34.78) * mm, v(-1.36, 34.64) * mm, v(-1.16, 34.35) * mm, v(-0.93, 34) * mm, v(-0.76, 33.66) * mm, v(-0.62, 33.3) * mm, v(-0.54, 32.95) * mm, v(-0.53, 32.62) * mm, v(-0.58, 32.32) * mm, v(-0.74, 32.01) * mm, v(-0.97, 31.8) * mm, v(-1.16, 31.65) * mm, v(-1.28, 31.6) * mm, v(-1.32, 31.57) * mm]});
            skFitSpline(sketch, "E125", {"points": [v(5.2, 29.54) * mm, v(5.32, 29.49) * mm, v(5.66, 29.33) * mm, v(6.1, 28.97) * mm, v(6.55, 28.55) * mm, v(6.84, 28.05) * mm, v(7.08, 27.57) * mm, v(7.23, 27.05) * mm, v(7.28, 26.56) * mm, v(7.28, 26.22) * mm, v(7.28, 26.05) * mm]});
            skFitSpline(sketch, "E126", {"points": [v(7.28, 26.05) * mm, v(7.3, 26) * mm, v(7.36, 25.88) * mm, v(7.4, 25.76) * mm, v(7.41, 25.7) * mm]});
            skFitSpline(sketch, "E127", {"points": [v(7.41, 25.7) * mm, v(7.55, 25.61) * mm, v(7.88, 25.41) * mm, v(8.27, 25) * mm, v(8.6, 24.44) * mm, v(8.87, 23.87) * mm, v(8.97, 23.25) * mm, v(9, 22.67) * mm, v(8.93, 22.16) * mm, v(8.8, 21.67) * mm, v(8.61, 21.23) * mm, v(8.37, 20.8) * mm, v(8.16, 20.59) * mm, v(8.06, 20.5) * mm]});
            skFitSpline(sketch, "E128", {"points": [v(8.06, 20.5) * mm, v(8, 20.22) * mm, v(7.88, 19.68) * mm, v(7.67, 19.17) * mm, v(7.57, 18.93) * mm]});
            skFitSpline(sketch, "E129", {"points": [v(7.57, 18.93) * mm, v(7.5, 18.6) * mm, v(7.4, 18.1) * mm, v(7.14, 17.5) * mm, v(6.85, 17.1) * mm, v(6.57, 16.74) * mm, v(6.25, 16.44) * mm, v(5.92, 16.21) * mm, v(5.56, 15.98) * mm, v(5.3, 15.88) * mm, v(5.15, 15.82) * mm]});
            skFitSpline(sketch, "E130", {"points": [v(5.15, 15.82) * mm, v(5, 15.7) * mm, v(4.76, 15.5) * mm, v(4.36, 15.25) * mm, v(3.95, 15.01) * mm, v(3.44, 14.77) * mm, v(3.06, 14.63) * mm, v(2.86, 14.55) * mm]});
            skFitSpline(sketch, "E131", {"points": [v(2.86, 14.55) * mm, v(2.8, 14.46) * mm, v(2.64, 14.25) * mm, v(2.3, 14) * mm, v(1.89, 13.73) * mm, v(1.47, 13.52) * mm, v(1.02, 13.38) * mm, v(0.59, 13.3) * mm, v(0.24, 13.27) * mm, v(0.05, 13.27) * mm, v(0, 13.27) * mm]});
            skFitSpline(sketch, "E132", {"points": [v(2.86, 29.07) * mm, v(2.99, 29.11) * mm, v(3.34, 29.22) * mm, v(3.84, 29.23) * mm, v(4.4, 29.14) * mm, v(4.88, 28.98) * mm, v(5.34, 28.74) * mm, v(5.67, 28.44) * mm, v(5.95, 28.14) * mm, v(6.17, 27.84) * mm, v(6.34, 27.52) * mm, v(6.48, 27.17) * mm, v(6.57, 26.73) * mm, v(6.6, 26.33) * mm, v(6.58, 26.1) * mm, v(6.58, 26.02) * mm]});
            skFitSpline(sketch, "E133", {"points": [v(6.58, 26.02) * mm, v(6.57, 26) * mm, v(6.55, 25.97) * mm, v(6.45, 25.96) * mm, v(6.33, 26) * mm, v(6.1, 26.08) * mm, v(5.71, 26.34) * mm, v(5.04, 26.73) * mm, v(4.36, 27.34) * mm, v(3.67, 27.94) * mm, v(3.24, 28.41) * mm, v(2.98, 28.73) * mm, v(2.89, 28.88) * mm, v(2.85, 28.96) * mm, v(2.84, 29.01) * mm, v(2.83, 29.06) * mm, v(2.85, 29.07) * mm, v(2.86, 29.07) * mm]});
            skFitSpline(sketch, "E134", {"points": [v(0, 29.7) * mm, v(0.08, 29.7) * mm, v(0.28, 29.7) * mm, v(0.65, 29.66) * mm, v(1.02, 29.54) * mm, v(1.38, 29.4) * mm, v(1.68, 29.22) * mm, v(1.98, 29.01) * mm, v(2.2, 28.8) * mm, v(2.35, 28.6) * mm, v(2.4, 28.42) * mm, v(2.42, 28.3) * mm, v(2.42, 28.14) * mm, v(2.4, 27.99) * mm, v(2.3, 27.82) * mm, v(2.18, 27.65) * mm, v(2, 27.49) * mm, v(1.77, 27.35) * mm, v(1.5, 27.2) * mm, v(1.22, 27.1) * mm, v(0.91, 27.01) * mm, v(0.58, 26.95) * mm, v(0.27, 26.92) * mm, v(0.07, 26.91) * mm, v(0, 26.91) * mm]});
            skFitSpline(sketch, "E135", {"points": [v(6.85, 25.27) * mm, v(7, 25.18) * mm, v(7.37, 24.94) * mm, v(7.82, 24.47) * mm, v(8.1, 23.88) * mm, v(8.31, 23.3) * mm, v(8.3, 22.72) * mm, v(8.23, 22.17) * mm, v(8.1, 21.75) * mm, v(7.95, 21.5) * mm, v(7.88, 21.38) * mm]});
            skFitSpline(sketch, "E136", {"points": [v(6.85, 25.27) * mm, v(6.83, 25.27) * mm, v(6.78, 25.3) * mm, v(6.69, 25.28) * mm, v(6.6, 25.22) * mm, v(6.5, 25.11) * mm, v(6.46, 25.02) * mm, v(6.44, 24.97) * mm]});
            skFitSpline(sketch, "E137", {"points": [v(6.44, 24.97) * mm, v(6.41, 24.89) * mm, v(6.35, 24.73) * mm, v(6.3, 24.48) * mm, v(6.3, 24.21) * mm, v(6.3, 23.9) * mm, v(6.3, 23.57) * mm, v(6.31, 23.18) * mm, v(6.38, 22.74) * mm, v(6.46, 22.27) * mm, v(6.59, 21.85) * mm, v(6.73, 21.5) * mm, v(6.85, 21.21) * mm, v(7, 21.01) * mm, v(7.1, 20.88) * mm, v(7.23, 20.82) * mm, v(7.3, 20.78) * mm, v(7.37, 20.77) * mm, v(7.4, 20.8) * mm, v(7.45, 20.81) * mm, v(7.52, 20.89) * mm, v(7.63, 21) * mm, v(7.73, 21.15) * mm, v(7.82, 21.27) * mm, v(7.86, 21.35) * mm, v(7.88, 21.38) * mm]});
            skFitSpline(sketch, "E138", {"points": [v(0, 16.41) * mm, v(0, 16.41) * mm, v(0, 16.41) * mm, v(0, 16.41) * mm, v(0.32, 16.41) * mm, v(0.7, 16.38) * mm, v(1.13, 16.3) * mm, v(1.53, 16.22) * mm, v(1.85, 16.1) * mm, v(2.1, 16) * mm, v(2.26, 15.87) * mm, v(2.42, 15.75) * mm, v(2.52, 15.63) * mm, v(2.59, 15.5) * mm, v(2.59, 15.38) * mm, v(2.56, 15.27) * mm, v(2.53, 15.21) * mm, v(2.51, 15.18) * mm]});
            skFitSpline(sketch, "E139", {"points": [v(2.51, 15.18) * mm, v(2.49, 15.13) * mm, v(2.44, 15.05) * mm, v(2.31, 14.93) * mm, v(2.18, 14.77) * mm, v(1.99, 14.6) * mm, v(1.79, 14.46) * mm, v(1.57, 14.33) * mm, v(1.38, 14.22) * mm, v(1.2, 14.15) * mm, v(1.01, 14.08) * mm, v(0.75, 14.02) * mm, v(0.45, 13.96) * mm, v(0.19, 13.96) * mm, v(0.04, 13.97) * mm, v(0, 13.97) * mm]});
            skFitSpline(sketch, "E140", {"points": [v(6.3, 20.66) * mm, v(6.23, 20.68) * mm, v(6.03, 20.73) * mm, v(5.7, 20.7) * mm, v(5.36, 20.59) * mm, v(5.06, 20.45) * mm, v(4.78, 20.3) * mm, v(4.51, 20.09) * mm, v(4.28, 19.85) * mm, v(4.06, 19.62) * mm, v(3.86, 19.37) * mm, v(3.66, 19.13) * mm, v(3.5, 18.84) * mm, v(3.34, 18.56) * mm, v(3.21, 18.26) * mm, v(3.12, 17.94) * mm, v(3.05, 17.6) * mm, v(3.03, 17.28) * mm, v(3.06, 17.01) * mm, v(3.14, 16.75) * mm, v(3.31, 16.51) * mm, v(3.5, 16.35) * mm, v(3.64, 16.31) * mm, v(3.68, 16.3) * mm]});
            skFitSpline(sketch, "E141", {"points": [v(3.68, 16.3) * mm, v(3.73, 16.3) * mm, v(3.9, 16.3) * mm, v(4.17, 16.31) * mm, v(4.52, 16.35) * mm, v(4.83, 16.47) * mm, v(5.15, 16.57) * mm, v(5.46, 16.77) * mm, v(5.8, 17) * mm, v(6.1, 17.33) * mm, v(6.4, 17.7) * mm, v(6.62, 18.08) * mm, v(6.75, 18.46) * mm, v(6.84, 18.82) * mm, v(6.88, 19.2) * mm, v(6.9, 19.58) * mm, v(6.83, 19.95) * mm, v(6.74, 20.24) * mm, v(6.6, 20.45) * mm, v(6.46, 20.59) * mm, v(6.34, 20.64) * mm, v(6.3, 20.66) * mm]});
            skFitSpline(sketch, "E142", {"points": [v(3.44, 26.63) * mm, v(3.54, 26.6) * mm, v(3.76, 26.5) * mm, v(4.1, 26.31) * mm, v(4.47, 26.07) * mm, v(4.74, 25.7) * mm, v(5.05, 25.37) * mm, v(5.27, 24.93) * mm, v(5.45, 24.47) * mm, v(5.5, 23.98) * mm, v(5.51, 23.46) * mm, v(5.4, 22.93) * mm, v(5.17, 22.34) * mm, v(4.76, 21.89) * mm, v(4.25, 21.6) * mm, v(3.72, 21.45) * mm, v(3.2, 21.4) * mm, v(2.85, 21.47) * mm, v(2.7, 21.52) * mm]});
            skFitSpline(sketch, "E143", {"points": [v(2.7, 21.52) * mm, v(2.67, 21.52) * mm, v(2.5, 21.57) * mm, v(2.14, 21.71) * mm, v(1.68, 22.08) * mm, v(1.23, 22.5) * mm, v(0.88, 23.04) * mm, v(0.62, 23.65) * mm, v(0.51, 24.3) * mm, v(0.53, 24.94) * mm, v(0.72, 25.54) * mm, v(1.04, 26.05) * mm, v(1.46, 26.39) * mm, v(1.82, 26.6) * mm, v(2.16, 26.7) * mm, v(2.45, 26.74) * mm, v(2.7, 26.76) * mm, v(2.97, 26.75) * mm, v(3.15, 26.7) * mm, v(3.44, 26.63) * mm]});
            skFitSpline(sketch, "E144", {"points": [v(5.2, 29.54) * mm, v(5.2, 29.56) * mm, v(5.26, 29.6) * mm, v(5.42, 29.62) * mm, v(5.6, 29.7) * mm, v(5.8, 29.77) * mm, v(5.93, 29.9) * mm, v(5.99, 30.02) * mm, v(6.02, 30.1) * mm, v(6, 30.15) * mm, v(6, 30.17) * mm]});
            skFitSpline(sketch, "E145", {"points": [v(6, 30.17) * mm, v(6.11, 30.21) * mm, v(6.3, 30.28) * mm, v(6.53, 30.43) * mm, v(6.68, 30.58) * mm, v(6.74, 30.74) * mm, v(6.75, 30.83) * mm, v(6.75, 30.88) * mm]});
            skFitSpline(sketch, "E146", {"points": [v(6.75, 30.88) * mm, v(6.84, 30.94) * mm, v(6.99, 31.05) * mm, v(7.16, 31.21) * mm, v(7.3, 31.34) * mm, v(7.35, 31.49) * mm, v(7.37, 31.61) * mm, v(7.36, 31.7) * mm, v(7.35, 31.74) * mm]});
            skFitSpline(sketch, "E147", {"points": [v(7.35, 31.74) * mm, v(7.41, 31.79) * mm, v(7.52, 31.88) * mm, v(7.63, 32.03) * mm, v(7.7, 32.17) * mm, v(7.73, 32.32) * mm, v(7.73, 32.46) * mm, v(7.72, 32.54) * mm, v(7.72, 32.58) * mm]});
            skFitSpline(sketch, "E148", {"points": [v(7.72, 32.58) * mm, v(7.77, 32.64) * mm, v(7.87, 32.75) * mm, v(7.97, 32.91) * mm, v(8.01, 33.07) * mm, v(8, 33.19) * mm, v(8.02, 33.3) * mm, v(7.99, 33.38) * mm, v(7.97, 33.41) * mm]});
            skFitSpline(sketch, "E149", {"points": [v(7.97, 33.41) * mm, v(8.02, 33.48) * mm, v(8.1, 33.6) * mm, v(8.15, 33.78) * mm, v(8.17, 33.93) * mm, v(8.16, 34.09) * mm, v(8.12, 34.22) * mm, v(8.05, 34.3) * mm, v(8.01, 34.35) * mm, v(8, 34.36) * mm]});
            skFitSpline(sketch, "E150", {"points": [v(8, 34.36) * mm, v(8.02, 34.39) * mm, v(8.06, 34.43) * mm, v(8.1, 34.53) * mm, v(8.12, 34.64) * mm, v(8.12, 34.77) * mm, v(8.13, 34.91) * mm, v(8.05, 35.05) * mm, v(7.96, 35.16) * mm, v(7.84, 35.24) * mm, v(7.72, 35.28) * mm, v(7.59, 35.3) * mm, v(7.46, 35.3) * mm, v(7.36, 35.28) * mm, v(7.3, 35.27) * mm, v(7.3, 35.27) * mm]});
            skFitSpline(sketch, "E151", {"points": [v(7.3, 35.27) * mm, v(7.28, 35.3) * mm, v(7.24, 35.36) * mm, v(7.17, 35.44) * mm, v(7.08, 35.53) * mm, v(6.97, 35.56) * mm, v(6.83, 35.6) * mm, v(6.66, 35.6) * mm, v(6.45, 35.61) * mm, v(6.3, 35.6) * mm, v(6.23, 35.6) * mm]});
            skFitSpline(sketch, "E152", {"points": [v(0, 33.27) * mm, v(0.04, 33.38) * mm, v(0.14, 33.6) * mm, v(0.27, 33.94) * mm, v(0.42, 34.26) * mm, v(0.62, 34.56) * mm, v(0.8, 34.83) * mm, v(1, 35.05) * mm, v(1.18, 35.22) * mm, v(1.36, 35.3) * mm, v(1.5, 35.34) * mm, v(1.62, 35.37) * mm, v(1.68, 35.35) * mm, v(1.7, 35.34) * mm]});
            skFitSpline(sketch, "E153", {"points": [v(1.7, 35.34) * mm, v(1.76, 35.4) * mm, v(1.88, 35.5) * mm, v(2.02, 35.64) * mm, v(2.15, 35.75) * mm, v(2.3, 35.77) * mm, v(2.43, 35.8) * mm, v(2.55, 35.78) * mm, v(2.64, 35.76) * mm, v(2.69, 35.75) * mm, v(2.71, 35.74) * mm]});
            skFitSpline(sketch, "E154", {"points": [v(2.71, 35.74) * mm, v(2.78, 35.78) * mm, v(2.88, 35.86) * mm, v(3.04, 35.93) * mm, v(3.18, 35.95) * mm, v(3.3, 35.95) * mm, v(3.43, 35.93) * mm, v(3.5, 35.9) * mm, v(3.54, 35.87) * mm]});
            skFitSpline(sketch, "E155", {"points": [v(3.54, 35.87) * mm, v(3.61, 35.9) * mm, v(3.74, 35.96) * mm, v(3.92, 36.03) * mm, v(4.1, 36.06) * mm, v(4.26, 36.07) * mm, v(4.4, 36.02) * mm, v(4.47, 35.96) * mm, v(4.5, 35.93) * mm]});
            skFitSpline(sketch, "E156", {"points": [v(4.5, 35.93) * mm, v(4.57, 35.95) * mm, v(4.7, 35.99) * mm, v(4.9, 36.04) * mm, v(5.07, 36.06) * mm, v(5.22, 36) * mm, v(5.35, 35.97) * mm, v(5.43, 35.9) * mm, v(5.46, 35.85) * mm, v(5.48, 35.83) * mm]});
            skFitSpline(sketch, "E157", {"points": [v(5.48, 35.83) * mm, v(5.53, 35.84) * mm, v(5.65, 35.86) * mm, v(5.82, 35.85) * mm, v(5.96, 35.82) * mm, v(6.08, 35.78) * mm, v(6.15, 35.72) * mm, v(6.2, 35.67) * mm, v(6.22, 35.62) * mm, v(6.23, 35.6) * mm]});
            skFitSpline(sketch, "E158", {"points": [v(1.68, 31.17) * mm, v(1.7, 31.05) * mm, v(1.74, 30.82) * mm, v(1.93, 30.57) * mm, v(2.1, 30.36) * mm, v(2.33, 30.19) * mm, v(2.6, 30.04) * mm, v(2.94, 29.92) * mm, v(3.3, 29.83) * mm, v(3.7, 29.75) * mm, v(4.09, 29.74) * mm, v(4.41, 29.73) * mm, v(4.59, 29.74) * mm, v(4.63, 29.75) * mm]});
            skFitSpline(sketch, "E159", {"points": [v(4.63, 29.75) * mm, v(4.58, 29.78) * mm, v(4.48, 29.84) * mm, v(4.32, 29.9) * mm, v(4.29, 29.98) * mm, v(4.27, 30.01) * mm]});
            skFitSpline(sketch, "E160", {"points": [v(4.27, 30.01) * mm, v(4.34, 30.03) * mm, v(4.48, 30.06) * mm, v(4.72, 30.05) * mm, v(4.97, 30.08) * mm, v(5.2, 30.13) * mm, v(5.41, 30.15) * mm, v(5.48, 30.25) * mm, v(5.5, 30.28) * mm]});
            skFitSpline(sketch, "E161", {"points": [v(5.5, 30.28) * mm, v(5.46, 30.29) * mm, v(5.37, 30.3) * mm, v(5.26, 30.33) * mm, v(5.17, 30.36) * mm, v(5.13, 30.42) * mm, v(5.13, 30.46) * mm, v(5.13, 30.47) * mm]});
            skFitSpline(sketch, "E162", {"points": [v(5.13, 30.47) * mm, v(5.17, 30.48) * mm, v(5.27, 30.51) * mm, v(5.42, 30.53) * mm, v(5.61, 30.58) * mm, v(5.83, 30.64) * mm, v(6.03, 30.71) * mm, v(6.2, 30.82) * mm, v(6.23, 30.9) * mm, v(6.24, 30.93) * mm]});
            skFitSpline(sketch, "E163", {"points": [v(6.24, 30.93) * mm, v(6.21, 30.92) * mm, v(6.11, 30.89) * mm, v(5.94, 30.88) * mm, v(5.83, 30.94) * mm, v(5.77, 30.97) * mm]});
            skFitSpline(sketch, "E164", {"points": [v(5.77, 30.97) * mm, v(5.97, 31.06) * mm, v(6.35, 31.24) * mm, v(6.68, 31.5) * mm, v(6.85, 31.63) * mm]});
            skFitSpline(sketch, "E165", {"points": [v(6.85, 31.63) * mm, v(6.77, 31.63) * mm, v(6.62, 31.63) * mm, v(6.43, 31.6) * mm, v(6.36, 31.67) * mm, v(6.34, 31.69) * mm]});
            skFitSpline(sketch, "E166", {"points": [v(6.34, 31.69) * mm, v(6.49, 31.76) * mm, v(6.81, 31.94) * mm, v(7.07, 32.2) * mm, v(7.21, 32.35) * mm]});
            skFitSpline(sketch, "E167", {"points": [v(7.21, 32.35) * mm, v(7.13, 32.36) * mm, v(7, 32.36) * mm, v(6.83, 32.35) * mm, v(6.77, 32.39) * mm, v(6.75, 32.4) * mm]});
            skFitSpline(sketch, "E168", {"points": [v(6.75, 32.4) * mm, v(6.88, 32.5) * mm, v(7.17, 32.72) * mm, v(7.38, 33.02) * mm, v(7.5, 33.18) * mm]});
            skFitSpline(sketch, "E169", {"points": [v(7.5, 33.18) * mm, v(7.44, 33.17) * mm, v(7.32, 33.15) * mm, v(7.16, 33.14) * mm, v(7.05, 33.16) * mm, v(7.01, 33.2) * mm, v(7, 33.2) * mm]});
            skFitSpline(sketch, "E170", {"points": [v(7.68, 33.94) * mm, v(7.6, 33.94) * mm, v(7.47, 33.94) * mm, v(7.3, 33.9) * mm, v(7.2, 33.9) * mm, v(7.14, 33.9) * mm]});
            skFitSpline(sketch, "E171", {"points": [v(7.14, 33.9) * mm, v(7.18, 34.03) * mm, v(7.25, 34.25) * mm, v(7.44, 34.5) * mm, v(7.55, 34.66) * mm, v(7.6, 34.73) * mm]});
            skFitSpline(sketch, "E172", {"points": [v(7.6, 34.73) * mm, v(7.46, 34.74) * mm, v(7.22, 34.74) * mm, v(6.91, 34.74) * mm, v(6.7, 34.74) * mm, v(6.6, 34.77) * mm, v(6.56, 34.78) * mm]});
            skFitSpline(sketch, "E173", {"points": [v(6.56, 34.78) * mm, v(6.6, 34.83) * mm, v(6.66, 34.92) * mm, v(6.78, 34.99) * mm, v(6.81, 35.05) * mm, v(6.82, 35.06) * mm]});
            skFitSpline(sketch, "E174", {"points": [v(6.82, 35.06) * mm, v(6.74, 35.07) * mm, v(6.52, 35.1) * mm, v(6.2, 35.1) * mm, v(5.9, 35.05) * mm, v(5.73, 34.94) * mm, v(5.63, 34.91) * mm, v(5.6, 34.9) * mm]});
            skFitSpline(sketch, "E175", {"points": [v(5.6, 34.9) * mm, v(5.58, 34.95) * mm, v(5.54, 35.04) * mm, v(5.63, 35.15) * mm, v(5.73, 35.22) * mm, v(5.8, 35.27) * mm, v(5.85, 35.3) * mm, v(5.87, 35.32) * mm]});
            skFitSpline(sketch, "E176", {"points": [v(5.87, 35.32) * mm, v(5.78, 35.32) * mm, v(5.61, 35.31) * mm, v(5.41, 35.25) * mm, v(5.24, 35.22) * mm, v(5.09, 35.16) * mm, v(4.94, 35.12) * mm, v(4.84, 35.1) * mm, v(4.79, 35.09) * mm, v(4.77, 35.08) * mm]});
            skFitSpline(sketch, "E177", {"points": [v(4.77, 35.08) * mm, v(4.77, 35.12) * mm, v(4.77, 35.19) * mm, v(4.84, 35.3) * mm, v(4.94, 35.36) * mm, v(5.04, 35.43) * mm, v(5.1, 35.46) * mm, v(5.12, 35.48) * mm]});
            skFitSpline(sketch, "E178", {"points": [v(5.12, 35.48) * mm, v(5, 35.48) * mm, v(4.79, 35.47) * mm, v(4.52, 35.37) * mm, v(4.3, 35.28) * mm, v(4.15, 35.18) * mm, v(4.06, 35.12) * mm, v(4.02, 35.1) * mm]});
            skFitSpline(sketch, "E179", {"points": [v(4.02, 35.1) * mm, v(4, 35.14) * mm, v(3.96, 35.23) * mm, v(4.01, 35.35) * mm, v(4.1, 35.44) * mm, v(4.14, 35.5) * mm, v(4.17, 35.53) * mm]});
            skFitSpline(sketch, "E180", {"points": [v(4.17, 35.53) * mm, v(4.12, 35.52) * mm, v(4, 35.51) * mm, v(3.85, 35.44) * mm, v(3.71, 35.36) * mm, v(3.6, 35.26) * mm, v(3.46, 35.17) * mm, v(3.35, 35.07) * mm, v(3.28, 35.01) * mm, v(3.25, 34.99) * mm]});
            skFitSpline(sketch, "E181", {"points": [v(3.25, 34.99) * mm, v(3.23, 35.03) * mm, v(3.18, 35.12) * mm, v(3.18, 35.28) * mm, v(3.24, 35.37) * mm, v(3.26, 35.42) * mm]});
            skFitSpline(sketch, "E182", {"points": [v(3.26, 35.42) * mm, v(3.2, 35.4) * mm, v(3.1, 35.36) * mm, v(2.94, 35.26) * mm, v(2.81, 35.13) * mm, v(2.73, 35.04) * mm, v(2.7, 35) * mm]});
            skFitSpline(sketch, "E183", {"points": [v(2.7, 35) * mm, v(2.67, 34.98) * mm, v(2.62, 34.91) * mm, v(2.57, 34.84) * mm, v(2.54, 34.8) * mm]});
            skFitSpline(sketch, "E184", {"points": [v(2.54, 34.8) * mm, v(2.51, 34.85) * mm, v(2.46, 34.93) * mm, v(2.42, 35.07) * mm, v(2.45, 35.18) * mm, v(2.46, 35.24) * mm, v(2.46, 35.26) * mm]});
            skFitSpline(sketch, "E185", {"points": [v(2.46, 35.26) * mm, v(2.4, 35.22) * mm, v(2.26, 35.14) * mm, v(2.1, 34.95) * mm, v(1.95, 34.78) * mm, v(1.8, 34.63) * mm, v(1.74, 34.52) * mm, v(1.7, 34.46) * mm]});
            skFitSpline(sketch, "E186", {"points": [v(1.7, 34.46) * mm, v(1.68, 34.5) * mm, v(1.61, 34.59) * mm, v(1.58, 34.72) * mm, v(1.58, 34.8) * mm, v(1.58, 34.82) * mm]});
            skFitSpline(sketch, "E187", {"points": [v(1.58, 34.82) * mm, v(1.53, 34.78) * mm, v(1.36, 34.64) * mm, v(1.16, 34.35) * mm, v(0.93, 34) * mm, v(0.76, 33.66) * mm, v(0.62, 33.3) * mm, v(0.54, 32.95) * mm, v(0.53, 32.62) * mm, v(0.58, 32.32) * mm, v(0.74, 32.01) * mm, v(0.97, 31.8) * mm, v(1.16, 31.65) * mm, v(1.28, 31.6) * mm, v(1.32, 31.57) * mm]});
            const initialGuessF9  = {"E54": [9.617094080744564e-05, 0.019522973925452138, -1, 0, 0.002723016135917339, 0.0023808498869806287, 4.747714, 1.5354706928204134], "E58": [-9.617165047286333e-05, 0.019522973925452138, 1, 0, 0.002723016135917339, 0.0023808498869806287, 4.747714614359173, 1.535471307179586]};
            skSetInitialGuess(sketch, initialGuessF9);
            skSolve(sketch);
        }
        {
            var Q0;
            Q0=makeQuery(id+"F9.imprint","IMPRINT",FACE,{"disambiguationData":[TD([[makeQuery(id+"F9.imprint","IMPRINT",EDGE,{"derivedFrom":sQuery(id+"F9.wireOp",EDGE,"E54")}),-1.0]])]});
            extrude(context, id + "F10", {"entities" : qUnion([Q0]), "operationType" : NewBodyOperationType.ADD, "depth" : 0.5 * mm, "offsetDistance" : 25 * mm});
        }
    });
